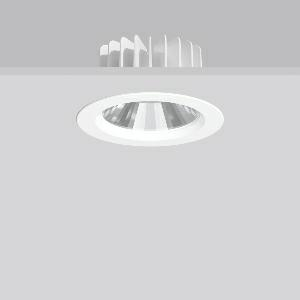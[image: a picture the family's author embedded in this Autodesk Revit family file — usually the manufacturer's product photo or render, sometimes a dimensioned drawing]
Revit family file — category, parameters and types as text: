
# Revit family: ledona_round_ip65_901793_002_76_3c51
name_source: partatom
category: Lighting Fixtures
units: mm (PartAtom-declared; Revit-internal decimal feet)

## family parameters
Cut with Voids When Loaded = No
Host = Face
Light Source = No
Part Type = Normal
Room Calculation Point = No
Round Connector Dimension = Use Diameter
Shared = No

## types (1)
- MultiLumen 1 (1 x LED Modul 930, 1450 lm, 3000)
    Apparent Load = 12 VA
    Approval mark = CE
    CIE Flux Codes = 94 99 100 100 100
    Color Rendering = 90
    Color Temperature = 3000
    Default Elevation = 1800 mm
    Height = 0 mm  [stored 0 ft]
    Lamp = 1 x LED Modul 930
    Lamp Light Flux = 1450 lm
    Lamp count = 1
    Length = 140 mm  [stored 0.459318 ft]
    Lifetime = 50000 h
    Luminous efficacy = 121 lm/W
    Manufacturer = RZB
    ModVariant = No
    Model = 901793.002.76
    Mounting Place = Ceiling
    Mounting Type = Recessed
    Number of Poles = 1
    OnlyDefault = Yes
    Power Factor = 1
    Product Name = LEDONA round IP65
    Product group = Recessed downlights
    ProductGroupID = 402
    Protection Class = Protection class II
    Protection Degree = IP 65
    RLX_Detail_Level = 1
    RLX_Emergency_Light_Flux = 0 lm
    RLX_Emergency_Type = 0
    RLX_Emergency_Type_DB = No
    RlxData = <blob elided: 38693 chars, md5=af907e35>
    Socket = socket
    Standby Power = 0 W
    System Light Flux = 1450 lm
    System Power = 12 W
    Type Comments = MultiLumen 1
    Type Image = 901346.002.jpg
    URL = http://relux.com
    VarID = multilumen_1
    Voltage = 230 V
    Voltage Range = 220-240 V
    Weight = 0.00 kg
    Width = 0 mm  [stored 0 ft]

note: [stored X ft] marks values corroborated as IEEE doubles in the binary element streams (Revit-internal decimal feet)

## geometry (parser evidence)
native form markers: Blend x4, Sweep x9
no freeform markers — native parametric forms only
